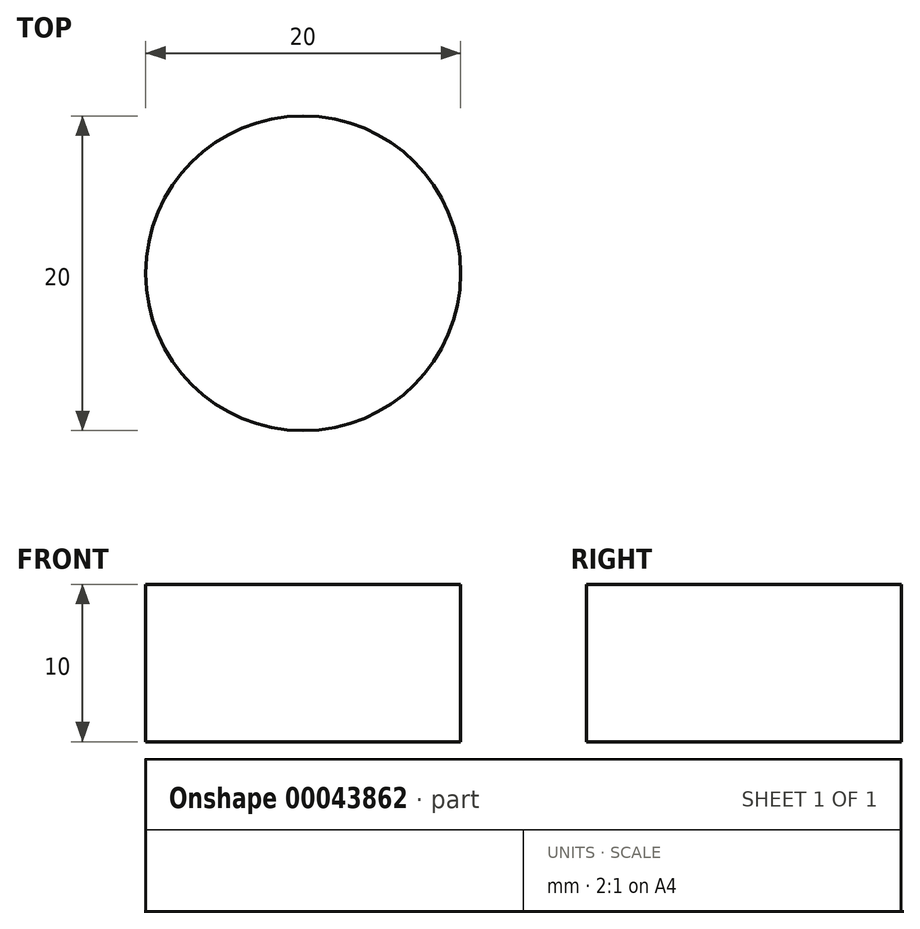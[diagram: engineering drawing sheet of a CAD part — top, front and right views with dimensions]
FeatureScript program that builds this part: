
annotation { "Feature Type Name" : "Feature", "Feature Type Description" : "" }
export const myFeature = defineFeature(function(context is Context, id is Id, definition is map)
    precondition{}
    {
        {
            var Q0;
            Q0=qCreatedBy(makeId("Top.planeOp"),FACE);
            var sketch = newSketch(context, id + "F0", { "sketchPlane" : qUnion([Q0])});
            skCircle(sketch, "E0", {"center": v(0, 0) * mm, "radius": 10 * mm});
            skSolve(sketch);
        }
        {
            var Q0;
            Q0 = qSketchRegion(id + "F0", true);
            extrude(context, id + "F1", {"entities" : qUnion([Q0]), "depth" : 10 * mm, "offsetDistance" : 25 * mm});
        }
    });
